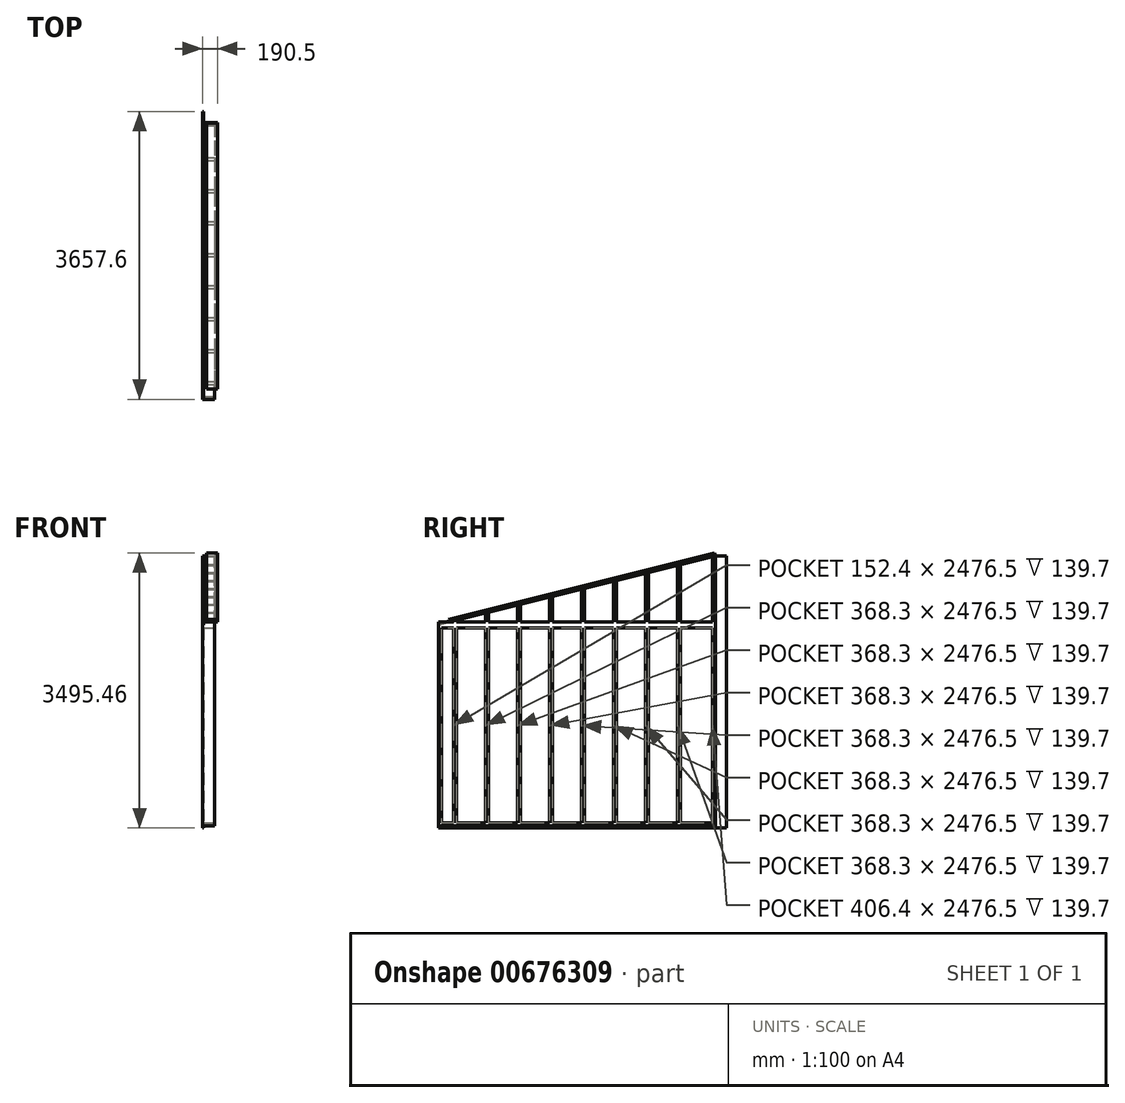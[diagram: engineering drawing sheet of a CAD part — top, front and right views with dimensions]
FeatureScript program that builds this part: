
annotation { "Feature Type Name" : "Feature", "Feature Type Description" : "" }
export const myFeature = defineFeature(function(context is Context, id is Id, definition is map)
    precondition{}
    {
        {
            var Q0;
            Q0=qCreatedBy(makeId("Top.planeOp"),FACE);
            var sketch = newSketch(context, id + "F0", { "sketchPlane" : qUnion([Q0])});
            skLineSegment(sketch, "E0.bottom", {"start": v(-69.85, 1758.95) * mm, "end": v(69.85, 1758.95) * mm});
            skLineSegment(sketch, "E0.top", {"start": v(-69.85, -1758.95) * mm, "end": v(69.85, -1758.95) * mm});
            skLineSegment(sketch, "E0.left", {"start": v(-69.85, 1758.95) * mm, "end": v(-69.85, -1758.95) * mm});
            skLineSegment(sketch, "E0.right", {"start": v(69.85, 1758.95) * mm, "end": v(69.85, -1758.95) * mm});
            skPoint(sketch, "E0.middle", {"position": v(0, 0) * mm});
            skSolve(sketch);
        }
        {
            var Q0;
            Q0=qSketchRegion(id+"F0",true);
            extrude(context, id + "F1", {"entities" : qUnion([Q0]), "depth" : 38.1 * mm, "offsetDistance" : 25.4 * mm});
        }
        {
            var Q0;
            Q0=makeQuery(id+"F1.opExtrude","SWEPT_FACE",FACE,{"disambiguationData":[OSD([sQuery(id+"F0.wireOp",EDGE,"E0.right")])]});
            var sketch = newSketch(context, id + "F2", { "sketchPlane" : qUnion([Q0])});
            skLineSegment(sketch, "E1.bottom", {"start": v(-1758.95, 38.1) * mm, "end": v(1758.95, 38.1) * mm, "construction": true});
            skLineSegment(sketch, "E1.top", {"start": v(-1758.95, 2590.8) * mm, "end": v(1720.85, 2590.8) * mm});
            skLineSegment(sketch, "E1.left", {"start": v(-1758.95, 38.1) * mm, "end": v(-1758.95, 2590.8) * mm});
            skLineSegment(sketch, "E1.right", {"start": v(1758.95, 38.1) * mm, "end": v(1758.95, 2590.8) * mm});
            skLineSegment(sketch, "E2.0", {"start": v(1720.85, 38.1) * mm, "end": v(1720.85, 2514.6) * mm});
            skLineSegment(sketch, "E3.0", {"start": v(-1720.85, 38.1) * mm, "end": v(-1720.85, 2514.6) * mm});
            skLineSegment(sketch, "E4.0", {"start": v(-1720.85, 2514.6) * mm, "end": v(1720.85, 2514.6) * mm});
            skLineSegment(sketch, "E5", {"start": v(1720.85, 38.1) * mm, "end": v(1758.95, 38.1) * mm});
            skLineSegment(sketch, "E6", {"start": v(-1720.85, 38.1) * mm, "end": v(-1758.95, 38.1) * mm});
            skLineSegment(sketch, "E7", {"start": v(1758.95, 2590.8) * mm, "end": v(1758.95, 3433.09) * mm});
            skLineSegment(sketch, "E8", {"start": v(1720.85, 3423.6) * mm, "end": v(-1619.25, 2590.83) * mm});
            skLineSegment(sketch, "E9", {"start": v(-1619.25, 2590.83) * mm, "end": v(-1628.47, 2627.8) * mm});
            skLineSegment(sketch, "E10", {"start": v(-1628.47, 2627.8) * mm, "end": v(1749.73, 3470.06) * mm});
            skLineSegment(sketch, "E11", {"start": v(1749.73, 3470.06) * mm, "end": v(1758.95, 3433.09) * mm});
            skLineSegment(sketch, "E12", {"start": v(1720.85, 2590.8) * mm, "end": v(1720.85, 3423.6) * mm});
            skSolve(sketch);
        }
        {
            var Q0;
            Q0=qSketchRegion(id+"F2",true);
            var Q1;
            Q1=makeQuery(id+"F1.opExtrude","SWEPT_FACE",FACE,{"disambiguationData":[OSD([sQuery(id+"F0.wireOp",EDGE,"E0.left")])]});
            extrude(context, id + "F3", {"entities" : qUnion([Q0]), "operationType" : NewBodyOperationType.ADD, "endBound" : BoundingType.UP_TO_SURFACE, "oppositeDirection" : true, "depth" : 289.56 * mm, "endBoundEntityFace" : qUnion([Q1]), "offsetDistance" : 25.4 * mm});
        }
        {
            var Q0;
            Q0=makeQuery(id+"F1.opExtrude","CAP_FACE",FACE,{"disambiguationData":[OSD([sQuery(id+"F0.wireOp",EDGE,"E0.bottom"),sQuery(id+"F0.wireOp",EDGE,"E0.top"),sQuery(id+"F0.wireOp",EDGE,"E0.left"),sQuery(id+"F0.wireOp",EDGE,"E0.right")])],"isStart":false});
            var sketch = newSketch(context, id + "F4", { "sketchPlane" : qUnion([Q0])});
            skLineSegment(sketch, "E13.bottom", {"start": v(-69.85, 1276.35) * mm, "end": v(69.85, 1276.35) * mm});
            skLineSegment(sketch, "E13.top", {"start": v(-69.85, 1314.45) * mm, "end": v(69.85, 1314.45) * mm});
            skLineSegment(sketch, "E13.left", {"start": v(-69.85, 1276.35) * mm, "end": v(-69.85, 1314.45) * mm});
            skLineSegment(sketch, "E13.right", {"start": v(69.85, 1276.35) * mm, "end": v(69.85, 1314.45) * mm});
            skLineSegment(sketch, "E14.0.1.0", {"start": v(-69.85, 869.95) * mm, "end": v(69.85, 869.95) * mm});
            skLineSegment(sketch, "E14.0.1.1", {"start": v(-69.85, 908.05) * mm, "end": v(69.85, 908.05) * mm});
            skLineSegment(sketch, "E14.0.1.2", {"start": v(-69.85, 869.95) * mm, "end": v(-69.85, 908.05) * mm});
            skLineSegment(sketch, "E14.0.1.3", {"start": v(69.85, 869.95) * mm, "end": v(69.85, 908.05) * mm});
            skLineSegment(sketch, "E14.0.2.0", {"start": v(-69.85, 463.55) * mm, "end": v(69.85, 463.55) * mm});
            skLineSegment(sketch, "E14.0.2.1", {"start": v(-69.85, 501.65) * mm, "end": v(69.85, 501.65) * mm});
            skLineSegment(sketch, "E14.0.2.2", {"start": v(-69.85, 463.55) * mm, "end": v(-69.85, 501.65) * mm});
            skLineSegment(sketch, "E14.0.2.3", {"start": v(69.85, 463.55) * mm, "end": v(69.85, 501.65) * mm});
            skLineSegment(sketch, "E14.0.3.0", {"start": v(-69.85, 57.15) * mm, "end": v(69.85, 57.15) * mm});
            skLineSegment(sketch, "E14.0.3.1", {"start": v(-69.85, 95.25) * mm, "end": v(69.85, 95.25) * mm});
            skLineSegment(sketch, "E14.0.3.2", {"start": v(-69.85, 57.15) * mm, "end": v(-69.85, 95.25) * mm});
            skLineSegment(sketch, "E14.0.3.3", {"start": v(69.85, 57.15) * mm, "end": v(69.85, 95.25) * mm});
            skLineSegment(sketch, "E14.0.4.0", {"start": v(-69.85, -349.25) * mm, "end": v(69.85, -349.25) * mm});
            skLineSegment(sketch, "E14.0.4.1", {"start": v(-69.85, -311.15) * mm, "end": v(69.85, -311.15) * mm});
            skLineSegment(sketch, "E14.0.4.2", {"start": v(-69.85, -349.25) * mm, "end": v(-69.85, -311.15) * mm});
            skLineSegment(sketch, "E14.0.4.3", {"start": v(69.85, -349.25) * mm, "end": v(69.85, -311.15) * mm});
            skLineSegment(sketch, "E14.0.5.0", {"start": v(-69.85, -755.65) * mm, "end": v(69.85, -755.65) * mm});
            skLineSegment(sketch, "E14.0.5.1", {"start": v(-69.85, -717.55) * mm, "end": v(69.85, -717.55) * mm});
            skLineSegment(sketch, "E14.0.5.2", {"start": v(-69.85, -755.65) * mm, "end": v(-69.85, -717.55) * mm});
            skLineSegment(sketch, "E14.0.5.3", {"start": v(69.85, -755.65) * mm, "end": v(69.85, -717.55) * mm});
            skLineSegment(sketch, "E14.0.6.0", {"start": v(-69.85, -1162.05) * mm, "end": v(69.85, -1162.05) * mm});
            skLineSegment(sketch, "E14.0.6.1", {"start": v(-69.85, -1123.95) * mm, "end": v(69.85, -1123.95) * mm});
            skLineSegment(sketch, "E14.0.6.2", {"start": v(-69.85, -1162.05) * mm, "end": v(-69.85, -1123.95) * mm});
            skLineSegment(sketch, "E14.0.6.3", {"start": v(69.85, -1162.05) * mm, "end": v(69.85, -1123.95) * mm});
            skLineSegment(sketch, "E14.0.7.0", {"start": v(-69.85, -1568.45) * mm, "end": v(69.85, -1568.45) * mm});
            skLineSegment(sketch, "E14.0.7.1", {"start": v(-69.85, -1530.35) * mm, "end": v(69.85, -1530.35) * mm});
            skLineSegment(sketch, "E14.0.7.2", {"start": v(-69.85, -1568.45) * mm, "end": v(-69.85, -1530.35) * mm});
            skLineSegment(sketch, "E14.0.7.3", {"start": v(69.85, -1568.45) * mm, "end": v(69.85, -1530.35) * mm});
            skLineSegment(sketch, "E14.direction1", {"start": v(-69.85, 1276.35) * mm, "end": v(-44.45, 1276.35) * mm, "construction": true});
            skLineSegment(sketch, "E14.direction2", {"start": v(-69.85, 1276.35) * mm, "end": v(-69.85, 869.95) * mm, "construction": true});
            skSolve(sketch);
        }
        {
            var Q0;
            Q0 = qSketchRegion(id + "F4", true);
            var Q1;
            Q1=makeQuery(id+"F3.opExtrude","SWEPT_FACE",FACE,{"disambiguationData":[OSD([sQuery(id+"F2.wireOp",EDGE,"E8")])]});
            extrude(context, id + "F5", {"entities" : qUnion([Q0]), "operationType" : NewBodyOperationType.ADD, "endBound" : BoundingType.UP_TO_SURFACE, "depth" : 25.4 * mm, "endBoundEntityFace" : qUnion([Q1]), "offsetDistance" : 25.4 * mm});
        }
        {
            var Q0;
            Q0=makeQuery(id+"F3.opExtrude","SWEPT_FACE",FACE,{"disambiguationData":[OSD([sQuery(id+"F2.wireOp",EDGE,"E10")])]});
            var sketch = newSketch(context, id + "F6", { "sketchPlane" : qUnion([Q0])});
            skLineSegment(sketch, "E15.bottom", {"start": v(-69.85, -944.39) * mm, "end": v(-31.75, -944.39) * mm});
            skLineSegment(sketch, "E15.top", {"start": v(-69.85, 2537.23) * mm, "end": v(-31.75, 2537.23) * mm});
            skLineSegment(sketch, "E15.left", {"start": v(-69.85, -944.39) * mm, "end": v(-69.85, 2537.23) * mm});
            skLineSegment(sketch, "E15.right", {"start": v(-31.75, -944.39) * mm, "end": v(-31.75, 2537.23) * mm});
            skSolve(sketch);
        }
        {
            var Q0;
            Q0 = qSketchRegion(id + "F6", true);
            extrude(context, id + "F7", {"entities" : qUnion([Q0]), "operationType" : NewBodyOperationType.REMOVE, "oppositeDirection" : true, "depth" : 38.1 * mm, "offsetDistance" : 25.4 * mm});
        }
        {
            var Q0;
            Q0=makeQuery(id+"F5.boolean.opBoolean","MERGE",FACE,{"derivedFrom":[makeQuery(id+"F3.boolean.opBoolean","MERGE",FACE,{"derivedFrom":[makeQuery(id+"F1.opExtrude","SWEPT_FACE",FACE,{"disambiguationData":[OSD([sQuery(id+"F0.wireOp",EDGE,"E0.right")])]}),makeQuery(id+"F3.opExtrude","CAP_FACE",FACE,{"disambiguationData":[OSD([sQuery(id+"F2.wireOp",EDGE,"E1.top"),sQuery(id+"F2.wireOp",EDGE,"E1.left"),sQuery(id+"F2.wireOp",EDGE,"E1.right"),sQuery(id+"F2.wireOp",EDGE,"E2.0"),sQuery(id+"F2.wireOp",EDGE,"E3.0"),sQuery(id+"F2.wireOp",EDGE,"E4.0"),sQuery(id+"F2.wireOp",EDGE,"E5"),sQuery(id+"F2.wireOp",EDGE,"E6"),sQuery(id+"F2.wireOp",EDGE,"E7"),sQuery(id+"F2.wireOp",EDGE,"E8"),sQuery(id+"F2.wireOp",EDGE,"E9"),sQuery(id+"F2.wireOp",EDGE,"E10"),sQuery(id+"F2.wireOp",EDGE,"E11"),sQuery(id+"F2.wireOp",EDGE,"E12")])],"isStart":true})]}),makeQuery(id+"F5.opExtrude","SWEPT_FACE",FACE,{"disambiguationData":[OSD([sQuery(id+"F4.wireOp",EDGE,"E13.right")])]}),makeQuery(id+"F5.opExtrude","SWEPT_FACE",FACE,{"disambiguationData":[OSD([sQuery(id+"F4.wireOp",EDGE,"E14.0.1.3")])]}),makeQuery(id+"F5.opExtrude","SWEPT_FACE",FACE,{"disambiguationData":[OSD([sQuery(id+"F4.wireOp",EDGE,"E14.0.2.3")])]}),makeQuery(id+"F5.opExtrude","SWEPT_FACE",FACE,{"disambiguationData":[OSD([sQuery(id+"F4.wireOp",EDGE,"E14.0.3.3")])]}),makeQuery(id+"F5.opExtrude","SWEPT_FACE",FACE,{"disambiguationData":[OSD([sQuery(id+"F4.wireOp",EDGE,"E14.0.4.3")])]}),makeQuery(id+"F5.opExtrude","SWEPT_FACE",FACE,{"disambiguationData":[OSD([sQuery(id+"F4.wireOp",EDGE,"E14.0.5.3")])]}),makeQuery(id+"F5.opExtrude","SWEPT_FACE",FACE,{"disambiguationData":[OSD([sQuery(id+"F4.wireOp",EDGE,"E14.0.6.3")])]}),makeQuery(id+"F5.opExtrude","SWEPT_FACE",FACE,{"disambiguationData":[OSD([sQuery(id+"F4.wireOp",EDGE,"E14.0.7.3")])]})]});
            var sketch = newSketch(context, id + "F8", { "sketchPlane" : qUnion([Q0])});
            skLineSegment(sketch, "E16", {"start": v(-1628.47, 2627.8) * mm, "end": v(-1619.25, 2590.83) * mm});
            skLineSegment(sketch, "E17", {"start": v(-1619.25, 2590.83) * mm, "end": v(1758.95, 3433.09) * mm});
            skLineSegment(sketch, "E18", {"start": v(1758.95, 3433.09) * mm, "end": v(1749.73, 3470.06) * mm});
            skLineSegment(sketch, "E19", {"start": v(1749.73, 3470.06) * mm, "end": v(-1628.47, 2627.8) * mm});
            skSolve(sketch);
        }
        {
            var Q0;
            Q0 = qSketchRegion(id + "F8", true);
            extrude(context, id + "F9", {"entities" : qUnion([Q0]), "operationType" : NewBodyOperationType.ADD, "depth" : 38.1 * mm, "offsetDistance" : 25.4 * mm});
        }
        {
            var Q0;
            {var subQ0=sQuery(id+"F0.wireOp",EDGE,"E0.left");Q0=makeQuery(id+"F5.boolean.opBoolean","MERGE",FACE,{"derivedFrom":[makeQuery(id+"F3.boolean.opBoolean","MERGE",FACE,{"derivedFrom":[makeQuery(id+"F1.opExtrude","SWEPT_FACE",FACE,{"disambiguationData":[OSD([subQ0])]}),makeQuery(id+"F3.opExtrude","CAP_FACE",FACE,{"disambiguationData":[OSD([subQ0])],"isStart":false})]}),makeQuery(id+"F5.opExtrude","SWEPT_FACE",FACE,{"disambiguationData":[OSD([sQuery(id+"F4.wireOp",EDGE,"E13.left")])]}),makeQuery(id+"F5.opExtrude","SWEPT_FACE",FACE,{"disambiguationData":[OSD([sQuery(id+"F4.wireOp",EDGE,"E14.0.1.2")])]}),makeQuery(id+"F5.opExtrude","SWEPT_FACE",FACE,{"disambiguationData":[OSD([sQuery(id+"F4.wireOp",EDGE,"E14.0.2.2")])]}),makeQuery(id+"F5.opExtrude","SWEPT_FACE",FACE,{"disambiguationData":[OSD([sQuery(id+"F4.wireOp",EDGE,"E14.0.3.2")])]}),makeQuery(id+"F5.opExtrude","SWEPT_FACE",FACE,{"disambiguationData":[OSD([sQuery(id+"F4.wireOp",EDGE,"E14.0.4.2")])]}),makeQuery(id+"F5.opExtrude","SWEPT_FACE",FACE,{"disambiguationData":[OSD([sQuery(id+"F4.wireOp",EDGE,"E14.0.5.2")])]}),makeQuery(id+"F5.opExtrude","SWEPT_FACE",FACE,{"disambiguationData":[OSD([sQuery(id+"F4.wireOp",EDGE,"E14.0.6.2")])]}),makeQuery(id+"F5.opExtrude","SWEPT_FACE",FACE,{"disambiguationData":[OSD([sQuery(id+"F4.wireOp",EDGE,"E14.0.7.2")])]})]});}
            var sketch = newSketch(context, id + "F10", { "sketchPlane" : qUnion([Q0])});
            skLineSegment(sketch, "E20", {"start": v(1758.95, -25.4) * mm, "end": v(1758.95, 2556) * mm});
            skLineSegment(sketch, "E21", {"start": v(1758.95, 2556) * mm, "end": v(-1758.95, 3433.09) * mm});
            skLineSegment(sketch, "E22", {"start": v(-1758.95, 3433.09) * mm, "end": v(-1898.65, 3433.09) * mm});
            skLineSegment(sketch, "E23", {"start": v(-1898.65, 3433.09) * mm, "end": v(-1898.65, 0) * mm});
            skLineSegment(sketch, "E24", {"start": v(1758.95, -25.4) * mm, "end": v(-1898.65, -25.4) * mm});
            skLineSegment(sketch, "E25", {"start": v(-1898.65, -25.4) * mm, "end": v(-1898.65, 0) * mm});
            skSolve(sketch);
        }
        {
            var Q0;
            Q0 = qSketchRegion(id + "F10", true);
            extrude(context, id + "F11", {"entities" : qUnion([Q0]), "operationType" : NewBodyOperationType.ADD, "depth" : 12.7 * mm, "offsetDistance" : 25.4 * mm});
        }
    });
